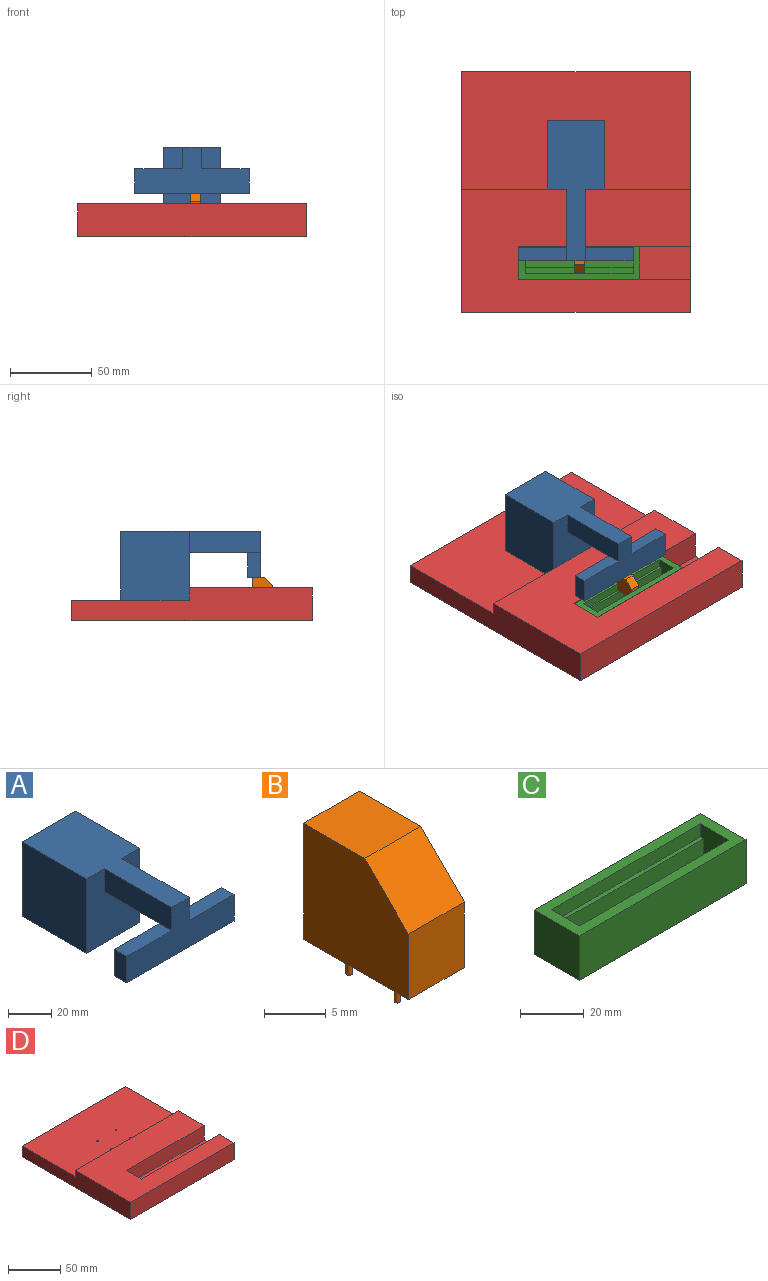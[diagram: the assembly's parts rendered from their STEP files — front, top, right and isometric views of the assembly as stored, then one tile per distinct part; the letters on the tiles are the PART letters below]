
ASSEMBLY  parts=4 mates=6
PART A: 16 faces, bbox 70x86x42 mm
  f0: plane 36x11.4mm, normal (0,0,-1), area 410.4mm2, adj f3,f7,f8,f12
  f1: plane 42x35mm, normal (0,1,0), area 1470mm2, adj f2,f4,f5,f6
  f2: plane 42x42mm, normal (-1,0,0), area 1764mm2, adj f1,f3,f5,f6
  f3: plane 42x35mm, normal (0,-1,0), area 1321.8mm2, adj f0,f2,f4,f5,f6,f7,f8
  f4: plane 42x42mm, normal (1,0,0), area 1764mm2, adj f1,f3,f5,f6
  f5: plane 86x35mm, normal (0,0,1), area 1971.6mm2, adj f1,f2,f3,f4,f7,f8,f9
  f6: plane 42x35mm, normal (0,0,-1), area 1470mm2, adj f1,f2,f3,f4
  f7: plane 44x13mm, normal (-1,0,0), area 572mm2, adj f0,f3,f5,f9,f10
  f8: plane 44x13mm, normal (1,0,0), area 572mm2, adj f0,f3,f5,f9,f15
  f9: plane 70x28mm, normal (0,-1,0), area 1198.2mm2, adj f5,f7,f8,f10,f11,f13,f14,f15
  f10: plane 29.3x8mm, normal (0,0,1), area 234.4mm2, adj f7,f9,f11,f12
  f11: plane 15x8mm, normal (-1,0,0), area 120mm2, adj f9,f10,f12,f14
  f12: plane 70x15mm, normal (0,1,0), area 1050mm2, adj f0,f10,f11,f13,f14,f15
  f13: plane 15x8mm, normal (1,0,0), area 120mm2, adj f9,f12,f14,f15
  f14: plane 70x8mm, normal (0,0,-1), area 560mm2, adj f9,f11,f12,f13
  f15: plane 29.3x8mm, normal (0,0,1), area 234.4mm2, adj f8,f9,f12,f13
PART B: 11 faces, bbox 6.4x12x15.5 mm
  f0: plane 7x6.4mm, normal (0,0,1), area 44.8mm2, adj f3,f4,f5,f10
  f1: plane 6.5x6.4mm, normal (0,-1,0), area 41.6mm2, adj f2,f4,f5,f10
  f2: plane 12x6.4mm, normal (0,0,-1), area 76.4mm2, adj f1,f3,f4,f5,f6,f8
  f3: plane 11.5x6.4mm, normal (0,1,0), area 73.6mm2, adj f0,f2,f4,f5
  f4: plane 12x11.5mm, normal (1,0,0), area 125.5mm2, adj f0,f1,f2,f3,f10
  f5: plane 12x11.5mm, normal (-1,0,0), area 125.5mm2, adj f0,f1,f2,f3,f10
  f6: cylinder r=0.25mm len=4mm, axis (0,0,1), area 6.3mm2, adj f2,f7
  f7: plane 0.5x0.5mm, normal (0,0,-1), area 0.2mm2, adj f6
  f8: cylinder r=0.25mm len=4mm, axis (0,0,1), area 6.3mm2, adj f2,f9
  f9: plane 0.5x0.5mm, normal (0,0,-1), area 0.2mm2, adj f8
  f10: plane 6.4x5mm, normal (0,-0.71,0.71), area 45.3mm2, adj f0,f1,f4,f5
PART C: 15 faces, bbox 74x20x17 mm
  f0: plane 66x8mm, normal (0,1,0), area 528mm2, adj f8,f9,f10,f14
  f1: plane 66x8mm, normal (0,-1,0), area 528mm2, adj f8,f9,f10,f11
  f2: plane 74x20mm, normal (0,0,1), area 655mm2, adj f3,f5,f6,f7,f9,f10,f12,f13
  f3: plane 74x17mm, normal (0,-1,0), area 1258mm2, adj f2,f4,f6,f7
  f4: plane 74x20mm, normal (0,0,-1), area 1480mm2, adj f3,f5,f6,f7
  f5: plane 74x17mm, normal (0,1,0), area 1258mm2, adj f2,f4,f6,f7
  f6: plane 20x17mm, normal (1,0,0), area 340mm2, adj f2,f3,f4,f5
  f7: plane 20x17mm, normal (-1,0,0), area 340mm2, adj f2,f3,f4,f5
  f8: plane 66x7.25mm, normal (0,0,1), area 478.5mm2, adj f0,f1,f9,f10
  f9: plane 13x12.5mm, normal (-1,0,0), area 120.5mm2, adj f0,f1,f2,f8,f11,f12,f13,f14
  f10: plane 13x12.5mm, normal (1,0,0), area 120.5mm2, adj f0,f1,f2,f8,f11,f12,f13,f14
  f11: plane 66x1.5mm, normal (0,0,1), area 99mm2, adj f1,f9,f10,f12
  f12: plane 66x5mm, normal (0,-1,0), area 330mm2, adj f2,f9,f10,f11
  f13: plane 66x5mm, normal (0,1,0), area 330mm2, adj f2,f9,f10,f14
  f14: plane 66x3.75mm, normal (0,0,1), area 247.5mm2, adj f0,f9,f10,f13
PART D: 20 faces, bbox 140x147.5x20 mm
  f0: plane 147.5x20mm, normal (-1,0,0), area 2410mm2, adj f2,f3,f4,f5,f10,f11
  f1: plane 105x17mm, normal (0,-1,0), area 1785mm2, adj f6,f8,f9,f10
  f2: plane 140x7.5mm, normal (0,1,0), area 1050mm2, adj f0,f6,f10,f11
  f3: plane 140x20mm, normal (0,-1,0), area 2800mm2, adj f0,f4,f6,f10
  f4: plane 147.5x140mm, normal (0,0,-1), area 20650mm2, adj f0,f3,f5,f6
  f5: plane 140x12.5mm, normal (0,1,0), area 1750mm2, adj f0,f4,f6,f11
  f6: plane 147.5x20mm, normal (1,0,0), area 2061.5mm2, adj f1,f2,f3,f4,f5,f7,f8,f10
  f7: plane 105x17mm, normal (0,1,0), area 1785mm2, adj f6,f8,f9,f10
  f8: plane 105x20.5mm, normal (0,0,1), area 2152.5mm2, adj f1,f6,f7,f9
  f9: plane 20.5x17mm, normal (1,0,0), area 348.5mm2, adj f1,f7,f8,f10
  f10: plane 140x75.5mm, normal (0,0,1), area 8417.5mm2, adj f0,f1,f2,f3,f6,f7,f9
  f11: plane 140x72mm, normal (0,0,1), area 10072mm2, adj f0,f2,f5,f6,f13,f15,f17,f19
  f12: cone r=0mm half-angle=59deg, axis (0,0,1), area 2.3mm2, adj f13
  f13: cylinder r=0.8mm len=6mm, axis (0,0,1), area 30.2mm2, adj f11,f12
  f14: cone r=0mm half-angle=59deg, axis (0,0,1), area 2.3mm2, adj f15
  f15: cylinder r=0.8mm len=6mm, axis (0,0,1), area 30.2mm2, adj f11,f14
  f16: cone r=0mm half-angle=59deg, axis (0,0,1), area 2.3mm2, adj f17
  f17: cylinder r=0.8mm len=6mm, axis (0,0,1), area 30.2mm2, adj f11,f16
  f18: cone r=0mm half-angle=59deg, axis (0,0,1), area 2.3mm2, adj f19
  f19: cylinder r=0.8mm len=6mm, axis (0,0,1), area 30.2mm2, adj f11,f18
PLACE A t=(-30.17,17.73,41.25)mm
PLACE B t=(-28.17,-48.52,49.5)mm
PLACE C t=(-28.17,-48.52,40.25)mm
PLACE D t=(-30.17,-38.77,38.5)mm
MATE planar C.f7 <-> D.f9  axis (-1,0,0) through (-65.17,-48.52,40.25)mm
MATE planar B.f3 <-> C.f12  axis (0,1,0) through (-28.17,-42.27,49.5)mm
MATE planar B.f2 <-> C.f14  axis (0,0,-1) through (-28.17,-48.27,43.75)mm
MATE planar D.f2 <-> A.f3  axis (0,1,0) through (-30.17,-3.27,48.75)mm
MATE planar C.f4 <-> D.f8  axis (0,0,-1) through (-28.17,-48.52,31.75)mm
MATE planar D.f11 <-> A.f6  axis (0,0,1) through (-30.17,32.75,41.25)mm
